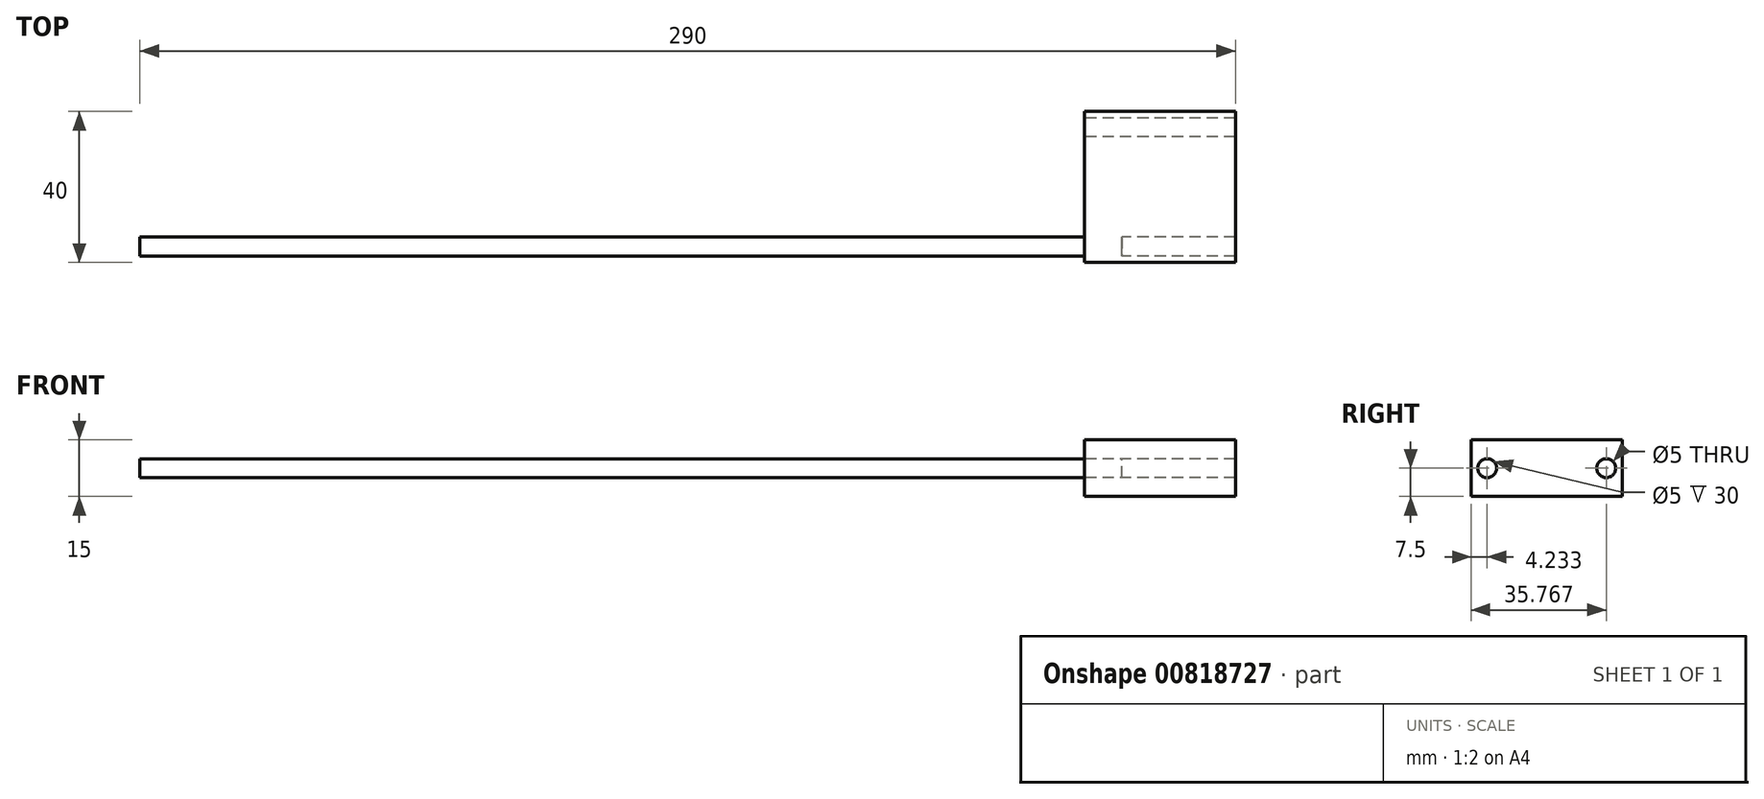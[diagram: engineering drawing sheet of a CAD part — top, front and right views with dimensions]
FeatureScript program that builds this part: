
annotation { "Feature Type Name" : "Feature", "Feature Type Description" : "" }
export const myFeature = defineFeature(function(context is Context, id is Id, definition is map)
    precondition{}
    {
        {
            var Q0;
            Q0=qCreatedBy(makeId("Right.planeOp"),FACE);
            var sketch = newSketch(context, id + "F0", { "sketchPlane" : qUnion([Q0])});
            skLineSegment(sketch, "E0.bottom", {"start": v(20, -7.5) * mm, "end": v(-20, -7.5) * mm});
            skLineSegment(sketch, "E0.top", {"start": v(20, 7.5) * mm, "end": v(-20, 7.5) * mm});
            skLineSegment(sketch, "E0.left", {"start": v(20, -7.5) * mm, "end": v(20, 7.5) * mm});
            skLineSegment(sketch, "E0.right", {"start": v(-20, -7.5) * mm, "end": v(-20, 7.5) * mm});
            skPoint(sketch, "E0.middle", {"position": v(0, 0) * mm});
            skCircle(sketch, "E1", {"center": v(-15.77, 0) * mm, "radius": 2.5 * mm});
            skLineSegment(sketch, "E2", {"start": v(0, -31.14) * mm, "end": v(0, 36.48) * mm, "construction": true});
            skCircle(sketch, "E3.MirrorC", {"center": v(15.77, 0) * mm, "radius": 2.5 * mm});
            skSolve(sketch);
        }
        {
            var Q0;
            Q0 = qSketchRegion(id + "F0", true);
            var Q1;
            Q1=makeQuery(id+"F0.imprint","IMPRINT",FACE,{"disambiguationData":[TD([[makeQuery(id+"F0.imprint","IMPRINT",EDGE,{"derivedFrom":sQuery(id+"F0.wireOp",EDGE,"E1")}),1.0]])]});
            extrude(context, id + "F1", {"entities" : qUnion([Q0, Q1]), "depth" : 10 * mm, "offsetDistance" : 25 * mm});
        }
        {
            var Q0;
            Q0=makeQuery(id+"F1.opExtrude","SWEPT_EDGE",EDGE,{"disambiguationData":[OSD([sQuery(id+"F0.wireOp",EDGE,"E0.top"),sQuery(id+"F0.wireOp",EDGE,"E0.right")])]});
            var Q1;
            Q1=makeQuery(id+"F1.opExtrude","SWEPT_EDGE",EDGE,{"disambiguationData":[OSD([sQuery(id+"F0.wireOp",EDGE,"E0.top"),sQuery(id+"F0.wireOp",EDGE,"E0.left")])]});
            var Q2;
            Q2=makeQuery(id+"F1.opExtrude","SWEPT_EDGE",EDGE,{"disambiguationData":[OSD([sQuery(id+"F0.wireOp",EDGE,"E0.bottom"),sQuery(id+"F0.wireOp",EDGE,"E0.right")])]});
            var Q3;
            Q3=makeQuery(id+"F1.opExtrude","SWEPT_EDGE",EDGE,{"disambiguationData":[OSD([sQuery(id+"F0.wireOp",EDGE,"E0.bottom"),sQuery(id+"F0.wireOp",EDGE,"E0.left")])]});
            fillet(context, id + "F2", {"entities" : qUnion([Q0, Q1, Q2, Q3]), "radius" : 5 * mm, "tangentPropagation" : true, "allowEdgeOverflow" : false});
        }
        {
            var Q0;
            Q0=makeQuery(id+"F0.imprint","IMPRINT",FACE,{"disambiguationData":[TD([[makeQuery(id+"F0.imprint","IMPRINT",EDGE,{"derivedFrom":sQuery(id+"F0.wireOp",EDGE,"E3.MirrorC")}),-1.0]])]});
            extrude(context, id + "F3", {"entities" : qUnion([Q0]), "operationType" : NewBodyOperationType.ADD, "depth" : 40 * mm, "offsetDistance" : 25 * mm});
        }
        {
            var Q0;
            Q0=makeQuery(id+"F0.imprint","IMPRINT",FACE,{"disambiguationData":[TD([[makeQuery(id+"F0.imprint","IMPRINT",EDGE,{"derivedFrom":sQuery(id+"F0.wireOp",EDGE,"E1")}),1.0]])]});
            extrude(context, id + "F4", {"entities" : qUnion([Q0]), "operationType" : NewBodyOperationType.ADD, "oppositeDirection" : true, "depth" : 250 * mm, "offsetDistance" : 25 * mm});
        }
    });
